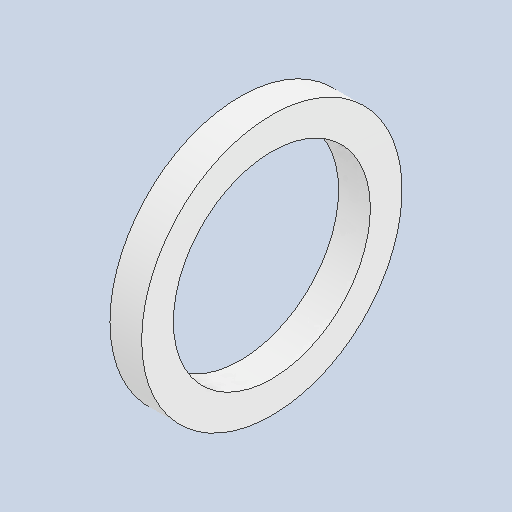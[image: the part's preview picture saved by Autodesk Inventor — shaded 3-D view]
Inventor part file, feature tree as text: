
AUTODESK INVENTOR PART (.ipt)
format: ipt  version: 2024.1 (Build 281209000, 209)  size: 92,160 bytes
history: native  units: in
note: dims shown in document units (in); Inventor stores cm internally (conversion verified against a paired STEP export)
features: revolve x1
ambient origin geometry x8: Origin, YZ Plane, XZ Plane, XY Plane, X Axis, Y Axis, Z Axis, Center Point
bodies: Solid1 (feature_tree)
feature tree (1):
  revolve  "Revolve1"  [1 undecoded]
note: 1 required parameter value undecoded (feature->parameter linkage not recoverable at this tier; creation-order binding heuristic only, values carry confidence <= 0.55)
